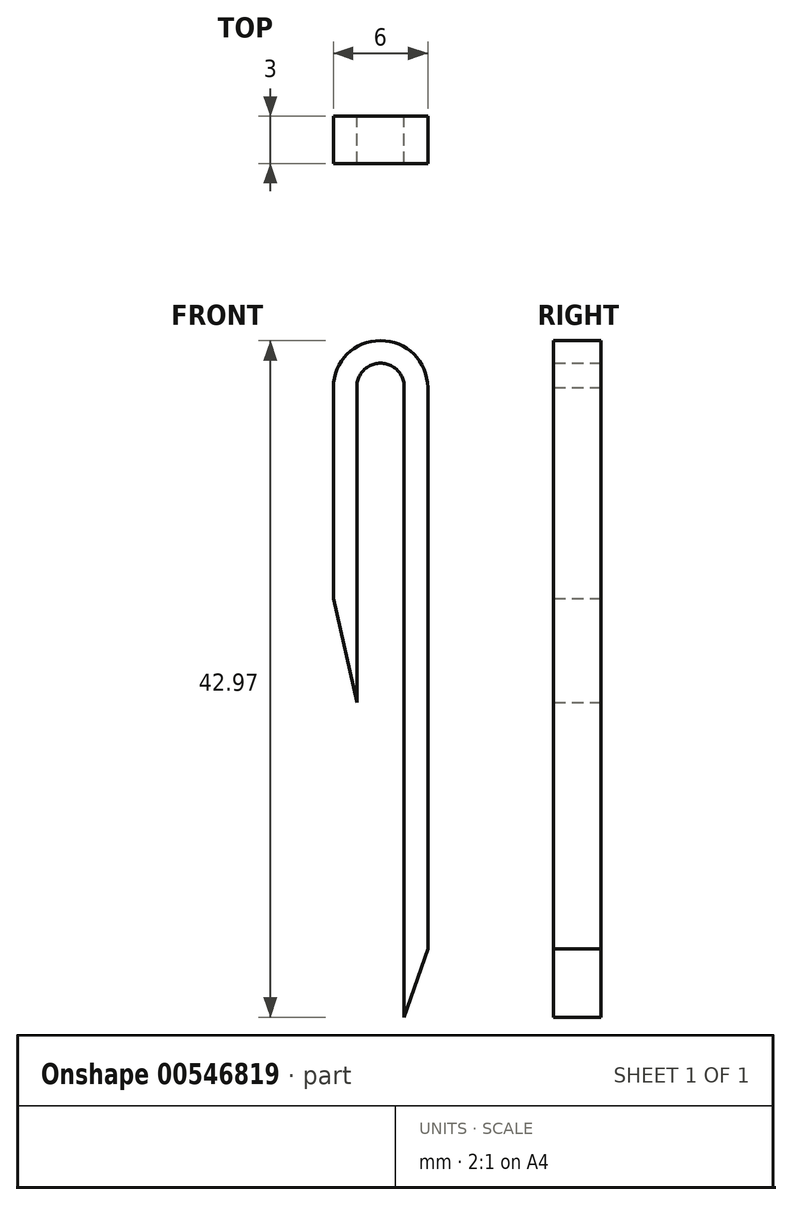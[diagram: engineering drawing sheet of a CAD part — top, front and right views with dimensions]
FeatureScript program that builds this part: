
annotation { "Feature Type Name" : "Feature", "Feature Type Description" : "" }
export const myFeature = defineFeature(function(context is Context, id is Id, definition is map)
    precondition{}
    {
        {
            var Q0;
            Q0=qCreatedBy(makeId("Front.planeOp"),FACE);
            var sketch = newSketch(context, id + "F0", { "sketchPlane" : qUnion([Q0])});
            skLineSegment(sketch, "E0", {"start": v(1.5, -40) * mm, "end": v(1.5, 0) * mm});
            skPoint(sketch, "E1.start.orphan", {"position": v(0, -40) * mm});
            skLineSegment(sketch, "E2", {"start": v(1.5, -40) * mm, "end": v(3, -35.66) * mm});
            skLineSegment(sketch, "E3", {"start": v(3, -35.66) * mm, "end": v(3, 0) * mm});
            skLineSegment(sketch, "E4.MirrorCS", {"start": v(-1.5, -20) * mm, "end": v(-1.5, 0) * mm});
            skLineSegment(sketch, "E5.MirrorCS", {"start": v(-3, -13.4) * mm, "end": v(-3, 0) * mm});
            skLineSegment(sketch, "E6", {"start": v(-1.5, -20) * mm, "end": v(-3, -13.4) * mm});
            skPoint(sketch, "E7.MirrorCS.end.orphan", {"position": v(-3, -35.66) * mm});
            skPoint(sketch, "E8.orphan", {"position": v(-1.5, -40) * mm});
            skArc(sketch, "E9", {"start": v(1.5, 0) * mm, "mid": v(0, 1.54) * mm, "end": v(-1.5, 0) * mm});
            skPoint(sketch, "E9.third.point", {"position": v(0, 1.54) * mm});
            skArc(sketch, "E10", {"start": v(3, -0.05) * mm, "mid": v(0, 2.97) * mm, "end": v(-3, -0.05) * mm});
            skPoint(sketch, "E10.third.point", {"position": v(0, 2.97) * mm});
            skSolve(sketch);
        }
        {
            var Q0;
            Q0=makeQuery(id+"F0.imprint","IMPRINT",FACE,{"disambiguationData":[TD([[makeQuery(id+"F0.imprint","IMPRINT",EDGE,{"derivedFrom":sQuery(id+"F0.wireOp",EDGE,"E0")}),-1.0]])]});
            extrude(context, id + "F1", {"entities" : qUnion([Q0]), "depth" : 3 * mm, "offsetDistance" : 25 * mm});
        }
    });
